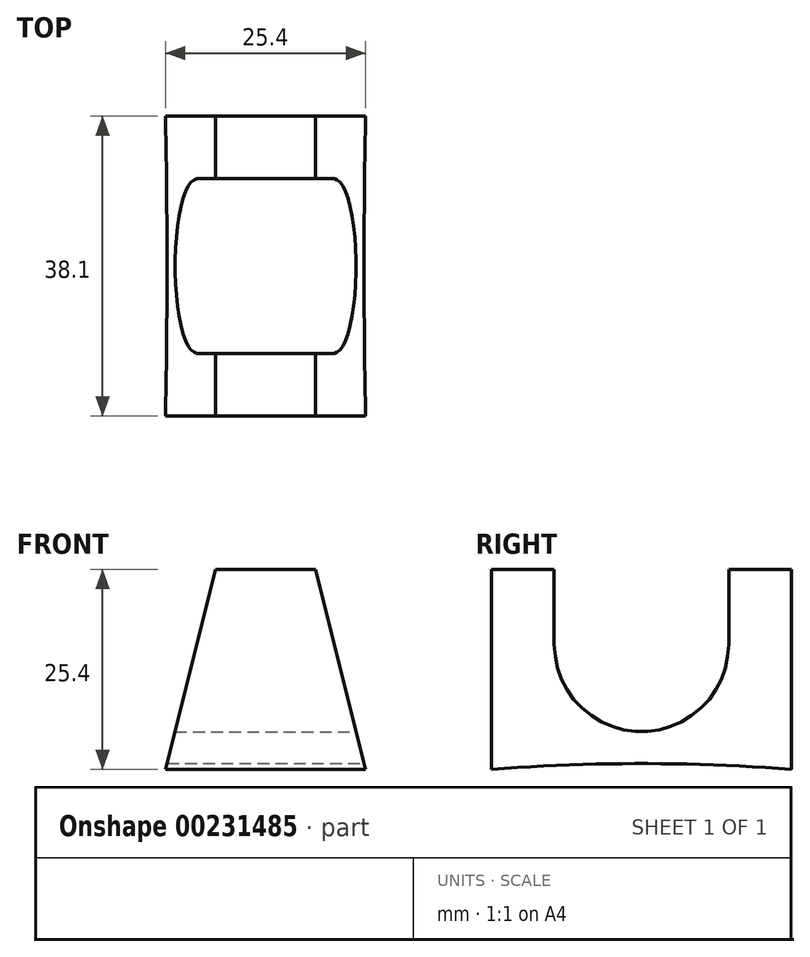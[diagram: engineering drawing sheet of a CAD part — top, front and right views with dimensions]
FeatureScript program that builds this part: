
annotation { "Feature Type Name" : "Feature", "Feature Type Description" : "" }
export const myFeature = defineFeature(function(context is Context, id is Id, definition is map)
    precondition{}
    {
        {
            var Q0;
            Q0=qCreatedBy(makeId("Front.planeOp"),FACE);
            var sketch = newSketch(context, id + "F0", { "sketchPlane" : qUnion([Q0])});
            skLineSegment(sketch, "E0", {"start": v(0, 0) * mm, "end": v(12.7, 0) * mm});
            skLineSegment(sketch, "E1", {"start": v(12.7, 0) * mm, "end": v(12.7, 25.4) * mm});
            skLineSegment(sketch, "E2", {"start": v(12.7, 25.4) * mm, "end": v(-12.7, 25.4) * mm});
            skLineSegment(sketch, "E3", {"start": v(-12.7, 25.4) * mm, "end": v(-12.7, 0) * mm});
            skLineSegment(sketch, "E4", {"start": v(-12.7, 0) * mm, "end": v(0, 0) * mm});
            skSolve(sketch);
        }
        {
            var Q0;
            Q0 = qSketchRegion(id + "F0", true);
            extrude(context, id + "F1", {"entities" : qUnion([Q0]), "depth" : 19.05 * mm});
        }
        {
            var Q0;
            Q0=makeQuery(id+"F1.opExtrude","CAP_FACE",FACE,{"disambiguationData":[OSD([sQuery(id+"F0.wireOp",EDGE,"E0"),sQuery(id+"F0.wireOp",EDGE,"E1"),sQuery(id+"F0.wireOp",EDGE,"E2"),sQuery(id+"F0.wireOp",EDGE,"E3"),sQuery(id+"F0.wireOp",EDGE,"E4")])],"isStart":true});
            extrude(context, id + "F2", {"entities" : qUnion([Q0]), "operationType" : NewBodyOperationType.ADD, "depth" : 19.05 * mm});
        }
        {
            var Q0;
            {var subQ0=sQuery(id+"F0.wireOp",EDGE,"E1");Q0=makeQuery(id+"F2.boolean.opBoolean","MERGE",FACE,{"derivedFrom":[makeQuery(id+"F1.opExtrude","SWEPT_FACE",FACE,{"disambiguationData":[OSD([subQ0])]}),makeQuery(id+"F2.opExtrude","SWEPT_FACE",FACE,{"disambiguationData":[OSD([subQ0])]})]});}
            var sketch = newSketch(context, id + "F3", { "sketchPlane" : qUnion([Q0])});
            skArc(sketch, "E5", {"start": v(19.05, 0) * mm, "mid": v(0, 0.74) * mm, "end": v(-19.05, 0) * mm});
            skPoint(sketch, "E5.centerSnap0", {"position": v(0, 0) * mm});
            skLineSegment(sketch, "E6", {"start": v(-19.05, 0) * mm, "end": v(19.05, 0) * mm});
            skSolve(sketch);
        }
        {
            var Q0;
            Q0 = qSketchRegion(id + "F3", true);
            extrude(context, id + "F4", {"entities" : qUnion([Q0]), "operationType" : NewBodyOperationType.REMOVE, "oppositeDirection" : true, "depth" : 25.4 * mm});
        }
        {
            var Q0;
            {var subQ0=sQuery(id+"F0.wireOp",EDGE,"E1");Q0=makeQuery(id+"F2.boolean.opBoolean","MERGE",FACE,{"derivedFrom":[makeQuery(id+"F1.opExtrude","SWEPT_FACE",FACE,{"disambiguationData":[OSD([subQ0])]}),makeQuery(id+"F2.opExtrude","SWEPT_FACE",FACE,{"disambiguationData":[OSD([subQ0])]})]});}
            var sketch = newSketch(context, id + "F5", { "sketchPlane" : qUnion([Q0])});
            skArc(sketch, "E7", {"start": v(-11.11, 15.88) * mm, "mid": v(0, 4.76) * mm, "end": v(11.11, 15.88) * mm});
            skLineSegment(sketch, "E8", {"start": v(11.11, 15.88) * mm, "end": v(11.11, 25.4) * mm});
            skLineSegment(sketch, "E9", {"start": v(-11.11, 15.88) * mm, "end": v(-11.11, 25.4) * mm});
            skLineSegment(sketch, "E10", {"start": v(-11.11, 25.4) * mm, "end": v(11.11, 25.4) * mm});
            skSolve(sketch);
        }
        {
            var Q0;
            Q0 = qSketchRegion(id + "F5", true);
            extrude(context, id + "F6", {"entities" : qUnion([Q0]), "operationType" : NewBodyOperationType.REMOVE, "oppositeDirection" : true, "depth" : 25.4 * mm});
        }
        {
            var Q0;
            Q0=makeQuery(id+"F1.opExtrude","CAP_FACE",FACE,{"disambiguationData":[OSD([sQuery(id+"F0.wireOp",EDGE,"E0"),sQuery(id+"F0.wireOp",EDGE,"E1"),sQuery(id+"F0.wireOp",EDGE,"E2"),sQuery(id+"F0.wireOp",EDGE,"E3"),sQuery(id+"F0.wireOp",EDGE,"E4")])],"isStart":false});
            var sketch = newSketch(context, id + "F7", { "sketchPlane" : qUnion([Q0])});
            skLineSegment(sketch, "E11", {"start": v(-12.7, 0) * mm, "end": v(-6.35, 25.4) * mm});
            skLineSegment(sketch, "E12", {"start": v(12.7, 0) * mm, "end": v(6.35, 25.4) * mm});
            skLineSegment(sketch, "E13", {"start": v(6.35, 25.4) * mm, "end": v(12.7, 25.4) * mm});
            skLineSegment(sketch, "E14", {"start": v(12.7, 25.4) * mm, "end": v(12.7, 0) * mm});
            skLineSegment(sketch, "E15", {"start": v(-12.7, 0) * mm, "end": v(-12.7, 25.4) * mm});
            skLineSegment(sketch, "E16", {"start": v(-12.7, 25.4) * mm, "end": v(-6.35, 25.4) * mm});
            skSolve(sketch);
        }
        {
            var Q0;
            Q0 = qSketchRegion(id + "F7", true);
            extrude(context, id + "F8", {"entities" : qUnion([Q0]), "operationType" : NewBodyOperationType.REMOVE, "oppositeDirection" : true, "depth" : 38.1 * mm});
        }
    });
